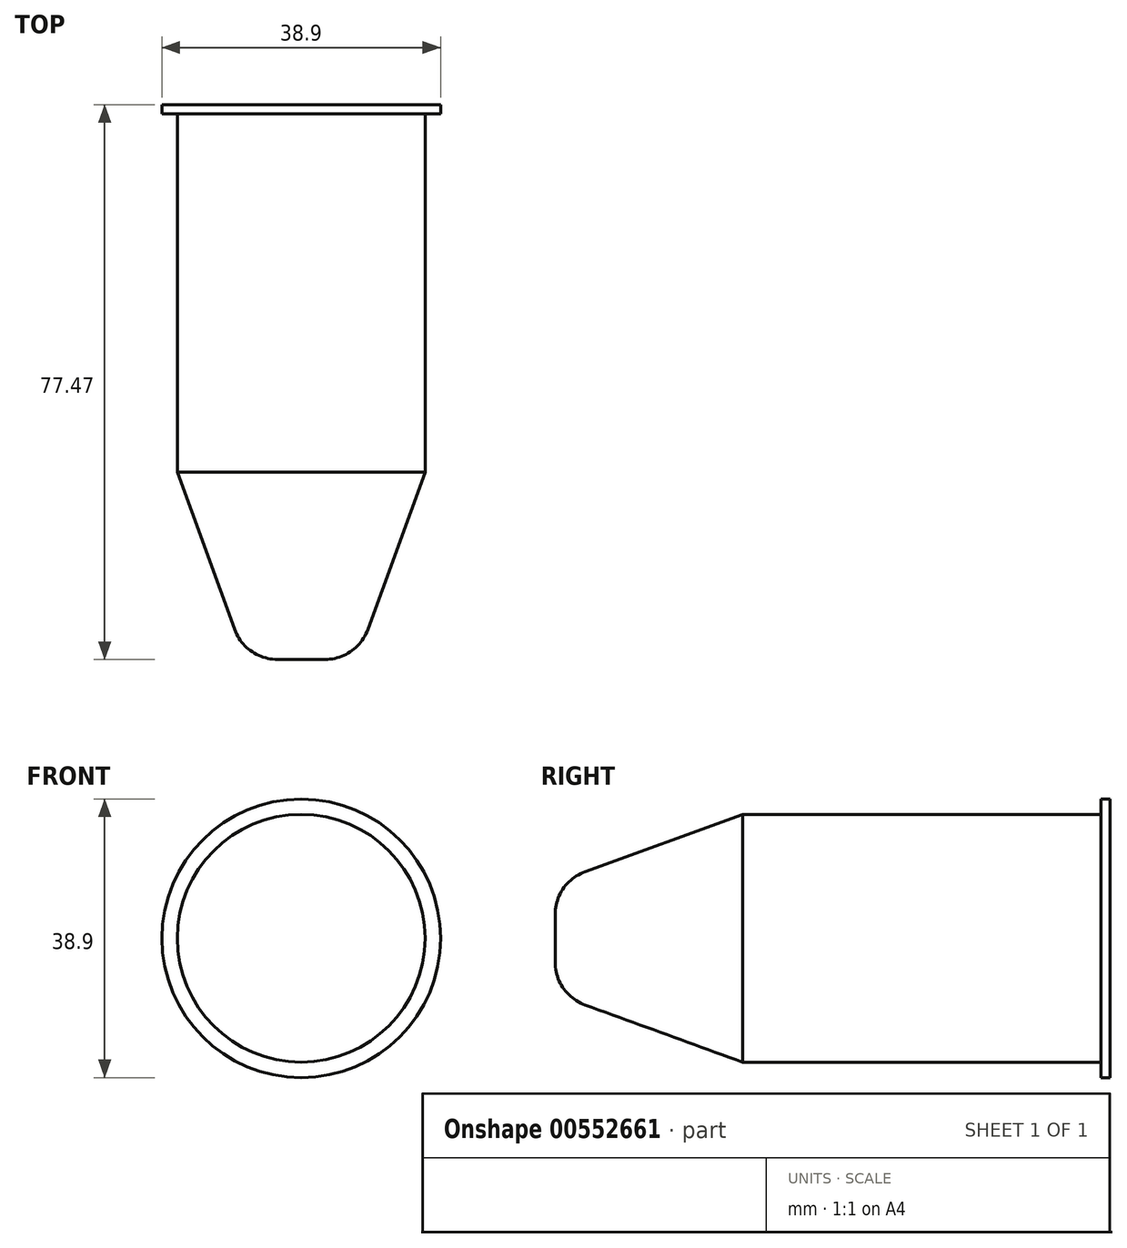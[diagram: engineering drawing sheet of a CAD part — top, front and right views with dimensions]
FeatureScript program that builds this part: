
annotation { "Feature Type Name" : "Feature", "Feature Type Description" : "" }
export const myFeature = defineFeature(function(context is Context, id is Id, definition is map)
    precondition{}
    {
        {
            var Q0;
            Q0=qCreatedBy(makeId("Front.planeOp"),FACE);
            var sketch = newSketch(context, id + "F0", { "sketchPlane" : qUnion([Q0])});
            skCircle(sketch, "E0", {"center": v(0, 0) * mm, "radius": 17.3 * mm});
            skSolve(sketch);
        }
        {
            var Q0;
            Q0 = qSketchRegion(id + "F0", true);
            extrude(context, id + "F1", {"entities" : qUnion([Q0]), "depth" : 76.2 * mm, "offsetDistance" : 25.4 * mm});
        }
        {
            var Q0;
            Q0=makeQuery(id+"F1.opExtrude","CAP_EDGE",EDGE,{"disambiguationData":[OSD([sQuery(id+"F0.wireOp",EDGE,"E0")])],"isStart":false});
            chamfer(context, id + "F2", {"entities" : qUnion([Q0]), "chamferType" : ChamferType.OFFSET_ANGLE, "width" : 9.52 * mm, "oppositeDirection" : false, "angle" : 70 * degree, "tangentPropagation" : true});
        }
        {
            var Q0;
            {var subQ0=sQuery(id+"F0.wireOp",EDGE,"E0");Q0=makeQuery(id+"F2.opChamfer","BLEND_EDGE",EDGE,{"blendedFrom":[makeQuery(id+"F1.opExtrude","CAP_EDGE",EDGE,{"disambiguationData":[OSD([subQ0])],"isStart":false}),makeQuery(id+"F1.opExtrude","CAP_FACE",FACE,{"disambiguationData":[OSD([subQ0])],"isStart":false})],"blendedInto":[makeQuery(id+"F1.opExtrude","CAP_FACE",FACE,{"disambiguationData":[OSD([subQ0])],"isStart":false})]});}
            fillet(context, id + "F3", {"entities" : qUnion([Q0]), "radius" : 6.35 * mm, "tangentPropagation" : true, "allowEdgeOverflow" : false});
        }
        {
            var Q0;
            Q0=makeQuery(id+"F1.opExtrude","CAP_FACE",FACE,{"disambiguationData":[OSD([sQuery(id+"F0.wireOp",EDGE,"E0")])],"isStart":true});
            var sketch = newSketch(context, id + "F4", { "sketchPlane" : qUnion([Q0])});
            skCircle(sketch, "E1", {"center": v(0, 0) * mm, "radius": 19.45 * mm});
            skSolve(sketch);
        }
        {
            var Q0;
            Q0 = qSketchRegion(id + "F4", true);
            extrude(context, id + "F5", {"entities" : qUnion([Q0]), "operationType" : NewBodyOperationType.ADD, "depth" : 1.27 * mm, "offsetDistance" : 25.4 * mm});
        }
    });
